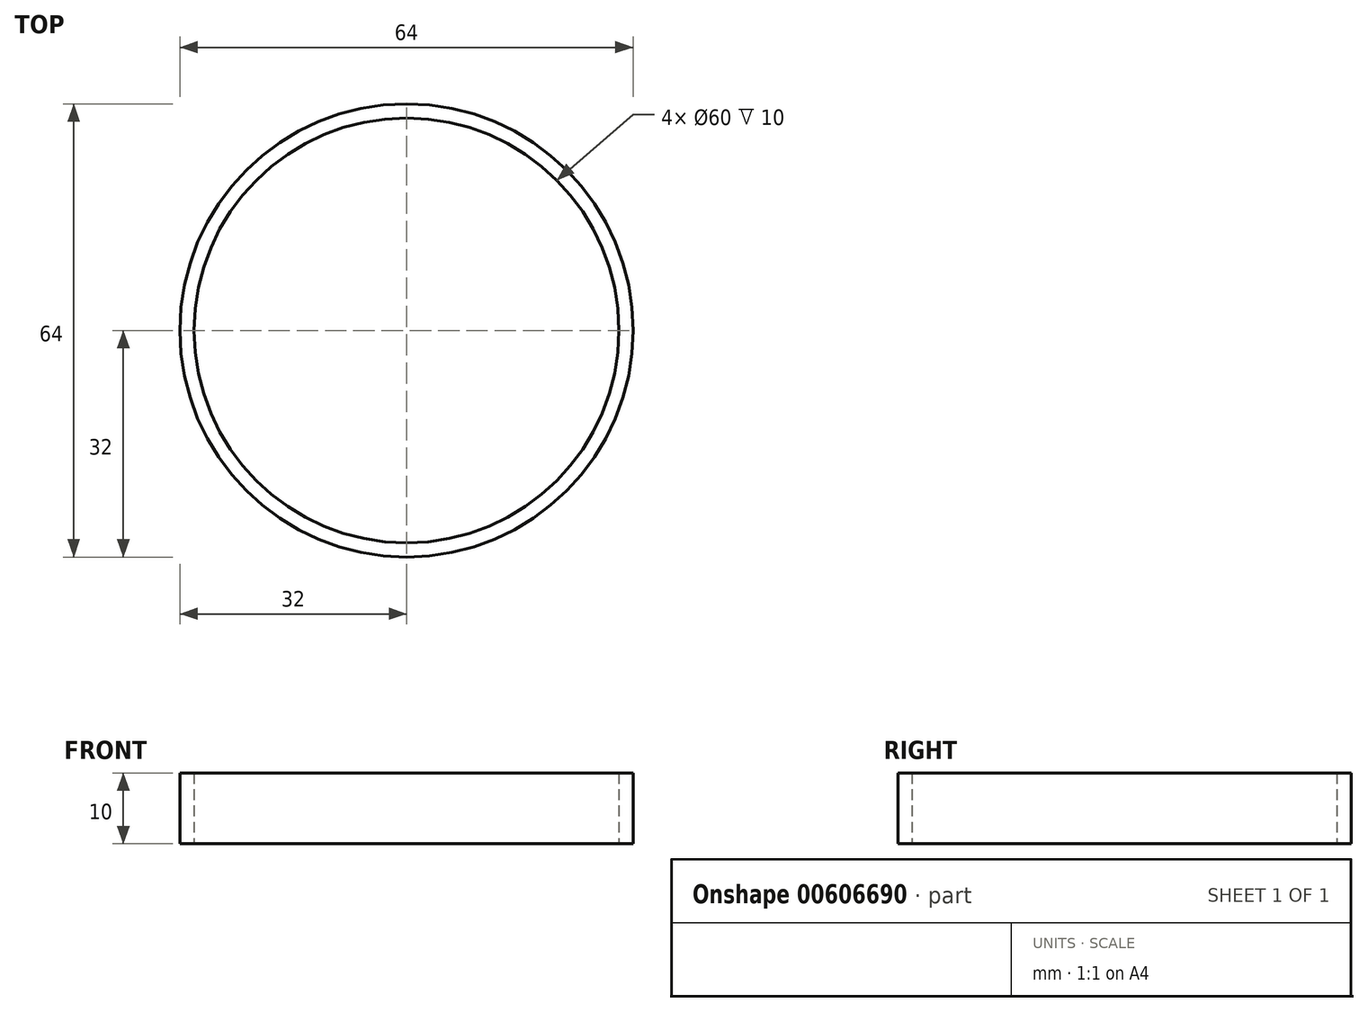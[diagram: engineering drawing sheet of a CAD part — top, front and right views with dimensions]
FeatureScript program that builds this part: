
annotation { "Feature Type Name" : "Feature", "Feature Type Description" : "" }
export const myFeature = defineFeature(function(context is Context, id is Id, definition is map)
    precondition{}
    {
        {
            var Q0;
            Q0=qCreatedBy(makeId("Top.planeOp"),FACE);
            var sketch = newSketch(context, id + "F0", { "sketchPlane" : qUnion([Q0])});
            skCircle(sketch, "E0", {"center": v(0, 0) * mm, "radius": 30 * mm});
            skCircle(sketch, "E1", {"center": v(0, 0) * mm, "radius": 32 * mm});
            skSolve(sketch);
        }
        {
            var Q0;
            Q0=makeQuery(id+"F0.imprint","IMPRINT",FACE,{"disambiguationData":[TD([[makeQuery(id+"F0.imprint","IMPRINT",EDGE,{"derivedFrom":sQuery(id+"F0.wireOp",EDGE,"E0")}),-1.0]])]});
            extrude(context, id + "F1", {"entities" : qUnion([Q0]), "depth" : 10 * mm, "offsetDistance" : 25 * mm});
        }
    });
